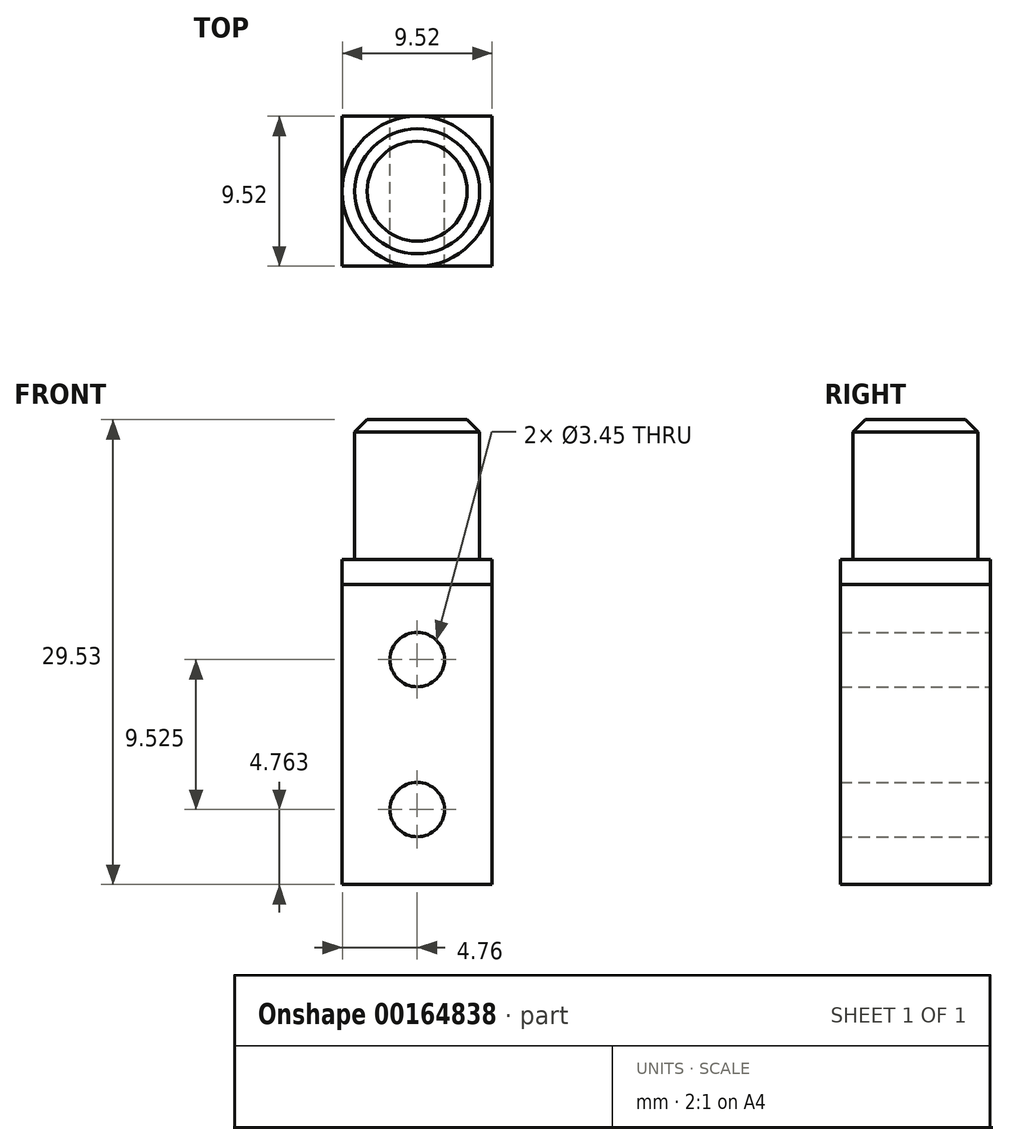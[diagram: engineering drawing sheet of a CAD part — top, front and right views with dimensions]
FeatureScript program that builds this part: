
annotation { "Feature Type Name" : "Feature", "Feature Type Description" : "" }
export const myFeature = defineFeature(function(context is Context, id is Id, definition is map)
    precondition{}
    {
        {
            var Q0;
            Q0=qCreatedBy(makeId("Top.planeOp"),FACE);
            var sketch = newSketch(context, id + "F0", { "sketchPlane" : qUnion([Q0])});
            skCircle(sketch, "E0", {"center": v(0, 0) * mm, "radius": 4.76 * mm});
            skSolve(sketch);
        }
        {
            var Q0;
            Q0 = qSketchRegion(id + "F0", true);
            extrude(context, id + "F1", {"entities" : qUnion([Q0]), "depth" : 1.59 * mm});
        }
        {
            var Q0;
            Q0=makeQuery(id+"F1.opExtrude","CAP_FACE",FACE,{"disambiguationData":[OSD([sQuery(id+"F0.wireOp",EDGE,"E0")])],"isStart":false});
            var sketch = newSketch(context, id + "F2", { "sketchPlane" : qUnion([Q0])});
            skCircle(sketch, "E1", {"center": v(0, 0) * mm, "radius": 3.97 * mm});
            skSolve(sketch);
        }
        {
            var Q0;
            Q0 = qSketchRegion(id + "F2", true);
            extrude(context, id + "F3", {"entities" : qUnion([Q0]), "operationType" : NewBodyOperationType.ADD, "depth" : 8.9 * mm});
        }
        {
            var Q0;
            Q0=makeQuery(id+"F1.opExtrude","CAP_FACE",FACE,{"disambiguationData":[OSD([sQuery(id+"F0.wireOp",EDGE,"E0")])],"isStart":true});
            var sketch = newSketch(context, id + "F4", { "sketchPlane" : qUnion([Q0])});
            skLineSegment(sketch, "E2.bottom", {"start": v(-4.76, -4.76) * mm, "end": v(4.76, -4.76) * mm});
            skLineSegment(sketch, "E2.top", {"start": v(-4.76, 4.76) * mm, "end": v(4.76, 4.76) * mm});
            skLineSegment(sketch, "E2.left", {"start": v(-4.76, -4.76) * mm, "end": v(-4.76, 4.76) * mm});
            skLineSegment(sketch, "E2.right", {"start": v(4.76, -4.76) * mm, "end": v(4.76, 4.76) * mm});
            skPoint(sketch, "E2.middle", {"position": v(0, 0) * mm});
            skSolve(sketch);
        }
        {
            var Q0;
            Q0 = qSketchRegion(id + "F4", true);
            extrude(context, id + "F5", {"entities" : qUnion([Q0]), "operationType" : NewBodyOperationType.ADD, "depth" : 19.05 * mm});
        }
        {
            var Q0;
            Q0=makeQuery(id+"F3.opExtrude","CAP_EDGE",EDGE,{"disambiguationData":[OSD([sQuery(id+"F2.wireOp",EDGE,"E1")])],"isStart":false});
            chamfer(context, id + "F6", {"entities" : qUnion([Q0]), "width" : 0.8 * mm, "tangentPropagation" : true});
        }
        {
            var Q0;
            Q0=makeQuery(id+"F5.opExtrude","SWEPT_FACE",FACE,{"disambiguationData":[OSD([sQuery(id+"F4.wireOp",EDGE,"E2.bottom")])]});
            var sketch = newSketch(context, id + "F7", { "sketchPlane" : qUnion([Q0])});
            skLineSegment(sketch, "E3.bottom", {"start": v(0, 0) * mm, "end": v(-4.76, 0) * mm, "construction": true});
            skLineSegment(sketch, "E3.top", {"start": v(0, -4.76) * mm, "end": v(-4.76, -4.76) * mm, "construction": true});
            skLineSegment(sketch, "E3.left", {"start": v(0, 0) * mm, "end": v(0, -4.76) * mm, "construction": true});
            skLineSegment(sketch, "E3.right", {"start": v(-4.76, 0) * mm, "end": v(-4.76, -4.76) * mm, "construction": true});
            skLineSegment(sketch, "E4.bottom", {"start": v(0, -19.05) * mm, "end": v(4.76, -19.05) * mm, "construction": true});
            skLineSegment(sketch, "E4.top", {"start": v(0, -14.29) * mm, "end": v(4.76, -14.29) * mm, "construction": true});
            skLineSegment(sketch, "E4.left", {"start": v(0, -19.05) * mm, "end": v(0, -14.29) * mm, "construction": true});
            skLineSegment(sketch, "E4.right", {"start": v(4.76, -19.05) * mm, "end": v(4.76, -14.29) * mm, "construction": true});
            skCircle(sketch, "E5", {"center": v(0, -4.76) * mm, "radius": 1.73 * mm});
            skCircle(sketch, "E6", {"center": v(0, -14.29) * mm, "radius": 1.73 * mm});
            skSolve(sketch);
        }
        {
            var Q0;
            Q0 = qSketchRegion(id + "F7", true);
            var Q1;
            Q1=makeQuery(id+"F5.opExtrude","SWEPT_FACE",FACE,{"disambiguationData":[OSD([sQuery(id+"F4.wireOp",EDGE,"E2.top")])]});
            extrude(context, id + "F8", {"entities" : qUnion([Q0]), "operationType" : NewBodyOperationType.REMOVE, "endBound" : BoundingType.UP_TO_SURFACE, "oppositeDirection" : true, "endBoundEntityFace" : qUnion([Q1]), "depth" : 25.4 * mm});
        }
    });
